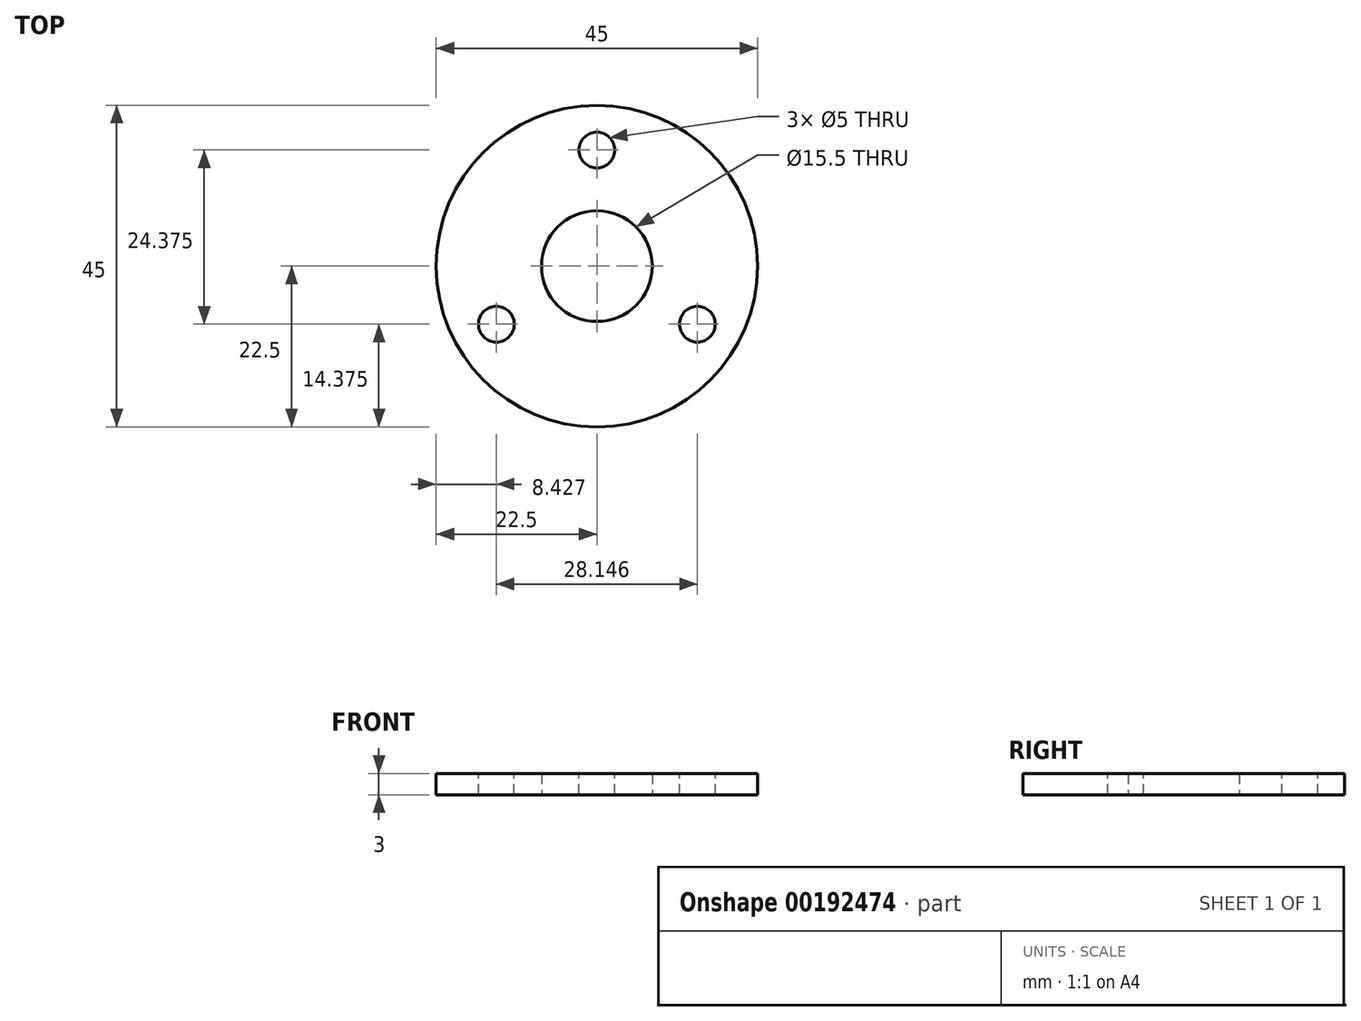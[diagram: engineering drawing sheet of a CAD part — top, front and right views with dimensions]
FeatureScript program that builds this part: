
annotation { "Feature Type Name" : "Feature", "Feature Type Description" : "" }
export const myFeature = defineFeature(function(context is Context, id is Id, definition is map)
    precondition{}
    {
        {
            var Q0;
            Q0=qCreatedBy(makeId("Top.planeOp"),FACE);
            var sketch = newSketch(context, id + "F0", { "sketchPlane" : qUnion([Q0])});
            skCircle(sketch, "E0", {"center": v(0, 0) * mm, "radius": 22.5 * mm});
            skCircle(sketch, "E1", {"center": v(0, 0) * mm, "radius": 7.75 * mm});
            skSolve(sketch);
        }
        {
            var Q0;
            Q0=makeQuery(id+"F0.imprint","IMPRINT",FACE,{"disambiguationData":[TD([[makeQuery(id+"F0.imprint","IMPRINT",EDGE,{"derivedFrom":sQuery(id+"F0.wireOp",EDGE,"E0")}),1.0]])]});
            extrude(context, id + "F1", {"entities" : qUnion([Q0]), "depth" : 3 * mm});
        }
        {
            var Q0;
            Q0=makeQuery(id+"F1.opExtrude","CAP_FACE",FACE,{"disambiguationData":[OSD([sQuery(id+"F0.wireOp",EDGE,"E0"),sQuery(id+"F0.wireOp",EDGE,"E1")])],"isStart":false});
            var sketch = newSketch(context, id + "F2", { "sketchPlane" : qUnion([Q0])});
            skCircle(sketch, "E2", {"center": v(0, 16.25) * mm, "radius": 2.5 * mm});
            skCircle(sketch, "E3.1.0", {"center": v(-14.07, -8.12) * mm, "radius": 2.5 * mm});
            skCircle(sketch, "E3.2.0", {"center": v(14.07, -8.12) * mm, "radius": 2.5 * mm});
            skPoint(sketch, "E3.center", {"position": v(0, 0) * mm});
            skSolve(sketch);
        }
        {
            var Q0;
            Q0=makeQuery(id+"F2.imprint","IMPRINT",FACE,{"disambiguationData":[TD([[makeQuery(id+"F2.imprint","IMPRINT",EDGE,{"derivedFrom":sQuery(id+"F2.wireOp",EDGE,"E3.2.0")}),1.0]])]});
            var Q1;
            Q1=makeQuery(id+"F2.imprint","IMPRINT",FACE,{"disambiguationData":[TD([[makeQuery(id+"F2.imprint","IMPRINT",EDGE,{"derivedFrom":sQuery(id+"F2.wireOp",EDGE,"E3.1.0")}),1.0]])]});
            var Q2;
            Q2=makeQuery(id+"F2.imprint","IMPRINT",FACE,{"disambiguationData":[TD([[makeQuery(id+"F2.imprint","IMPRINT",EDGE,{"derivedFrom":sQuery(id+"F2.wireOp",EDGE,"E2")}),1.0]])]});
            extrude(context, id + "F3", {"entities" : qUnion([Q0, Q1, Q2]), "operationType" : NewBodyOperationType.REMOVE, "oppositeDirection" : true, "depth" : 22.1 * mm});
        }
    });
